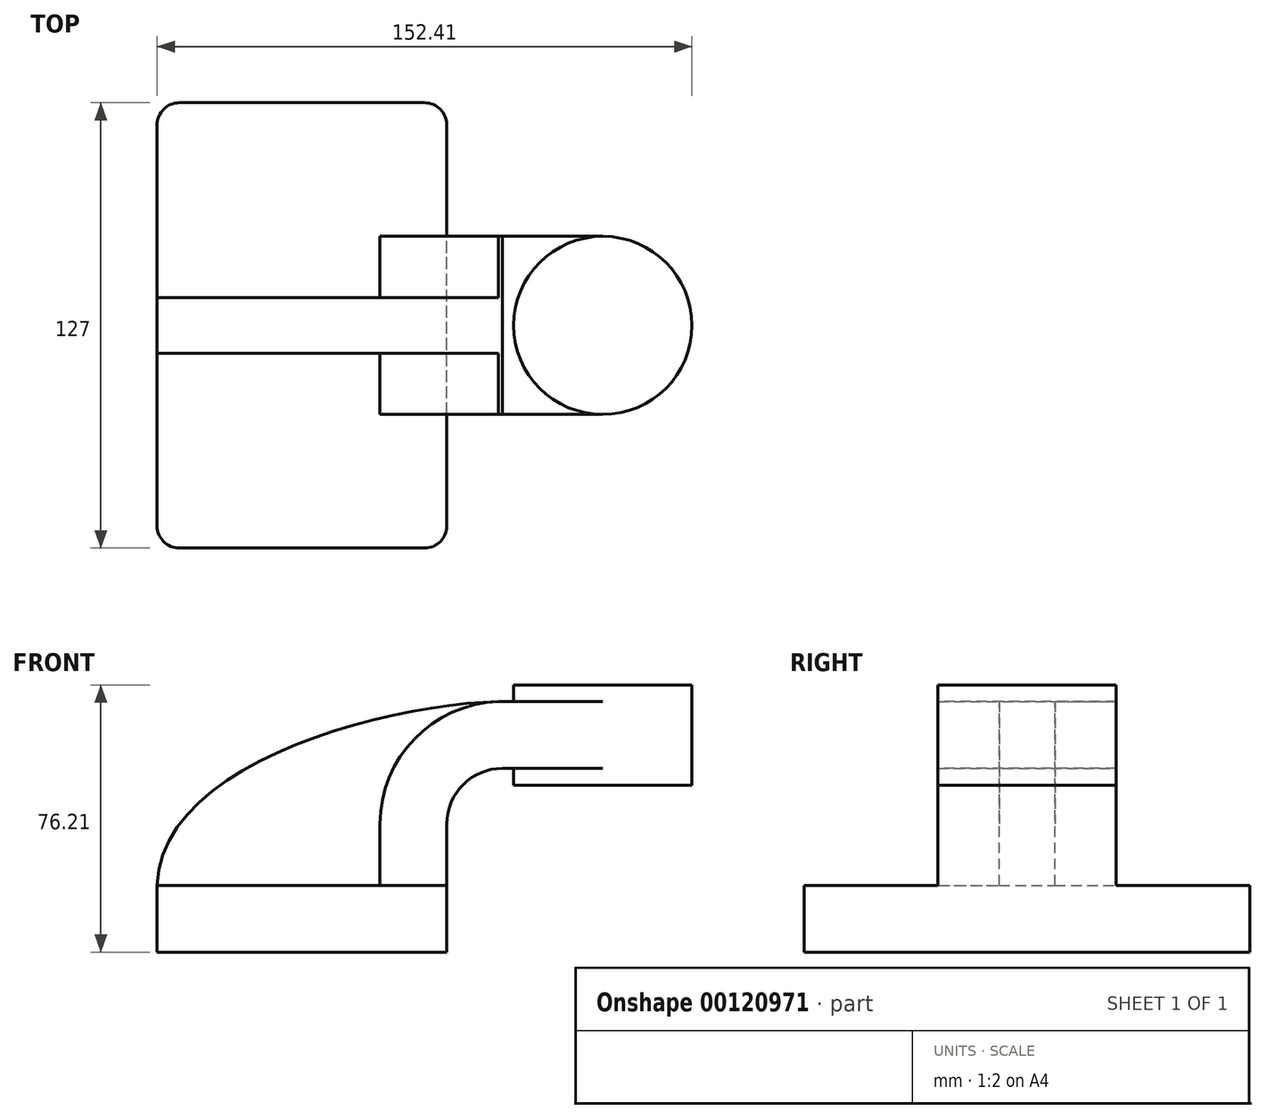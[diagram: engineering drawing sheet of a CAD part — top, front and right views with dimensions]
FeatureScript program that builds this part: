
annotation { "Feature Type Name" : "Feature", "Feature Type Description" : "" }
export const myFeature = defineFeature(function(context is Context, id is Id, definition is map)
    precondition{}
    {
        {
            var Q0;
            Q0=qCreatedBy(makeId("Front.planeOp"),FACE);
            var sketch = newSketch(context, id + "F0", { "sketchPlane" : qUnion([Q0])});
            skLineSegment(sketch, "E0.bottom", {"start": v(41.28, -9.52) * mm, "end": v(-41.28, -9.53) * mm});
            skLineSegment(sketch, "E0.top", {"start": v(41.28, 9.53) * mm, "end": v(-41.28, 9.52) * mm});
            skLineSegment(sketch, "E0.left", {"start": v(41.28, -9.52) * mm, "end": v(41.28, 9.53) * mm});
            skLineSegment(sketch, "E0.right", {"start": v(-41.28, -9.53) * mm, "end": v(-41.28, 9.52) * mm});
            skPoint(sketch, "E0.middle", {"position": v(0, 0) * mm});
            skLineSegment(sketch, "E1.bottom", {"start": v(111.12, 38.1) * mm, "end": v(60.33, 38.1) * mm});
            skLineSegment(sketch, "E1.top", {"start": v(111.13, 66.68) * mm, "end": v(60.32, 66.68) * mm});
            skLineSegment(sketch, "E1.left", {"start": v(111.12, 38.1) * mm, "end": v(111.12, 66.68) * mm});
            skLineSegment(sketch, "E1.right", {"start": v(60.33, 38.1) * mm, "end": v(60.33, 66.68) * mm});
            skPoint(sketch, "E1.middle", {"position": v(85.72, 52.39) * mm});
            skLineSegment(sketch, "E2", {"start": v(41.28, 9.53) * mm, "end": v(41.28, 27) * mm});
            skArc(sketch, "E3", {"start": v(41.28, 27) * mm, "mid": v(45.92, 38.23) * mm, "end": v(57.15, 42.88) * mm});
            skLineSegment(sketch, "E4", {"start": v(57.15, 42.88) * mm, "end": v(70.74, 42.88) * mm});
            skLineSegment(sketch, "E5", {"start": v(70.74, 42.88) * mm, "end": v(85.73, 42.88) * mm});
            skLineSegment(sketch, "E6.0", {"start": v(70.74, 61.93) * mm, "end": v(85.73, 61.93) * mm});
            skLineSegment(sketch, "E6.1", {"start": v(57.15, 61.93) * mm, "end": v(70.74, 61.93) * mm});
            skArc(sketch, "E6.2", {"start": v(22.23, 27) * mm, "mid": v(32.45, 51.7) * mm, "end": v(57.15, 61.93) * mm});
            skLineSegment(sketch, "E6.3", {"start": v(22.23, 9.53) * mm, "end": v(22.23, 27) * mm});
            skLineSegment(sketch, "E7", {"start": v(85.73, 61.93) * mm, "end": v(85.73, 42.88) * mm});
            skFitSpline(sketch, "E8", {"points": [v(-41.28, 9.53) * mm, v(57.15, 61.93) * mm], "startDerivative": vector(2.5, 105.53) * mm, "endDerivative": vector(95.74, 0.98) * mm});
            skLineSegment(sketch, "E9", {"start": v(85.72, 52.39) * mm, "end": v(85.72, 66.68) * mm});
            skLineSegment(sketch, "E10", {"start": v(85.73, 42.88) * mm, "end": v(85.73, 38.1) * mm});
            skSolve(sketch);
        }
        {
            var Q0;
            Q0=makeQuery(id+"F0.imprint","IMPRINT",FACE,{"disambiguationData":[TD([[makeQuery(id+"F0.imprint","IMPRINT",EDGE,{"derivedFrom":sQuery(id+"F0.wireOp",EDGE,"E0.bottom")}),-1.0]])]});
            extrude(context, id + "F1", {"entities" : qUnion([Q0]), "endBound" : BoundingType.SYMMETRIC, "depth" : 127 * mm});
        }
        {
            var Q0;
            {var subQ1=sQuery(id+"F0.wireOp",EDGE,"E2");Q0=makeQuery(id+"F0.imprint","IMPRINT",FACE,{"disambiguationData":[TD([[makeQuery(id+"F0.imprint","IMPRINT",EDGE,{"derivedFrom":subQ1}),1.0]])]});}
            var Q1;
            {var subQ1=sQuery(id+"F0.wireOp",EDGE,"E5");Q1=makeQuery(id+"F0.imprint","IMPRINT",FACE,{"disambiguationData":[TD([[makeQuery(id+"F0.imprint","IMPRINT",EDGE,{"derivedFrom":subQ1}),1.0]])]});}
            extrude(context, id + "F2", {"entities" : qUnion([Q0, Q1]), "operationType" : NewBodyOperationType.ADD, "endBound" : BoundingType.SYMMETRIC, "depth" : 50.8 * mm});
        }
        {
            var Q0;
            {var subQ3=sQuery(id+"F0.wireOp",EDGE,"E6.3");Q0=makeQuery(id+"F0.imprint","IMPRINT",FACE,{"disambiguationData":[TD([[makeQuery(id+"F0.imprint","IMPRINT",EDGE,{"derivedFrom":subQ3}),1.0]])]});}
            extrude(context, id + "F3", {"entities" : qUnion([Q0]), "operationType" : NewBodyOperationType.ADD, "endBound" : BoundingType.SYMMETRIC, "depth" : 15.88 * mm});
        }
        {
            var Q0;
            {var subQ1=sQuery(id+"F0.wireOp",EDGE,"E1.left");Q0=makeQuery(id+"F0.imprint","IMPRINT",FACE,{"disambiguationData":[TD([[makeQuery(id+"F0.imprint","IMPRINT",EDGE,{"derivedFrom":subQ1}),1.0]])]});}
            var Q1;
            Q1=sQuery(id+"F0.wireOp",EDGE,"E10");
            revolve(context, id + "F4", {"operationType" : NewBodyOperationType.ADD, "entities" : qUnion([Q0]), "axis" : qUnion([Q1]), "revolveType" : RevolveType.FULL});
        }
        {
            var Q0;
            Q0=makeQuery(id+"F1.opExtrude","CAP_EDGE",EDGE,{"disambiguationData":[OSD([sQuery(id+"F0.wireOp",EDGE,"E0.right")])],"isStart":false});
            var Q1;
            Q1=makeQuery(id+"F1.opExtrude","CAP_EDGE",EDGE,{"disambiguationData":[OSD([sQuery(id+"F0.wireOp",EDGE,"E0.left")])],"isStart":false});
            var Q2;
            Q2=makeQuery(id+"F1.opExtrude","CAP_EDGE",EDGE,{"disambiguationData":[OSD([sQuery(id+"F0.wireOp",EDGE,"E0.left")])],"isStart":true});
            var Q3;
            Q3=makeQuery(id+"F1.opExtrude","CAP_EDGE",EDGE,{"disambiguationData":[OSD([sQuery(id+"F0.wireOp",EDGE,"E0.right")])],"isStart":true});
            fillet(context, id + "F5", {"entities" : qUnion([Q0, Q1, Q2, Q3]), "radius" : 6.35 * mm, "tangentPropagation" : true, "allowEdgeOverflow" : false});
        }
    });
